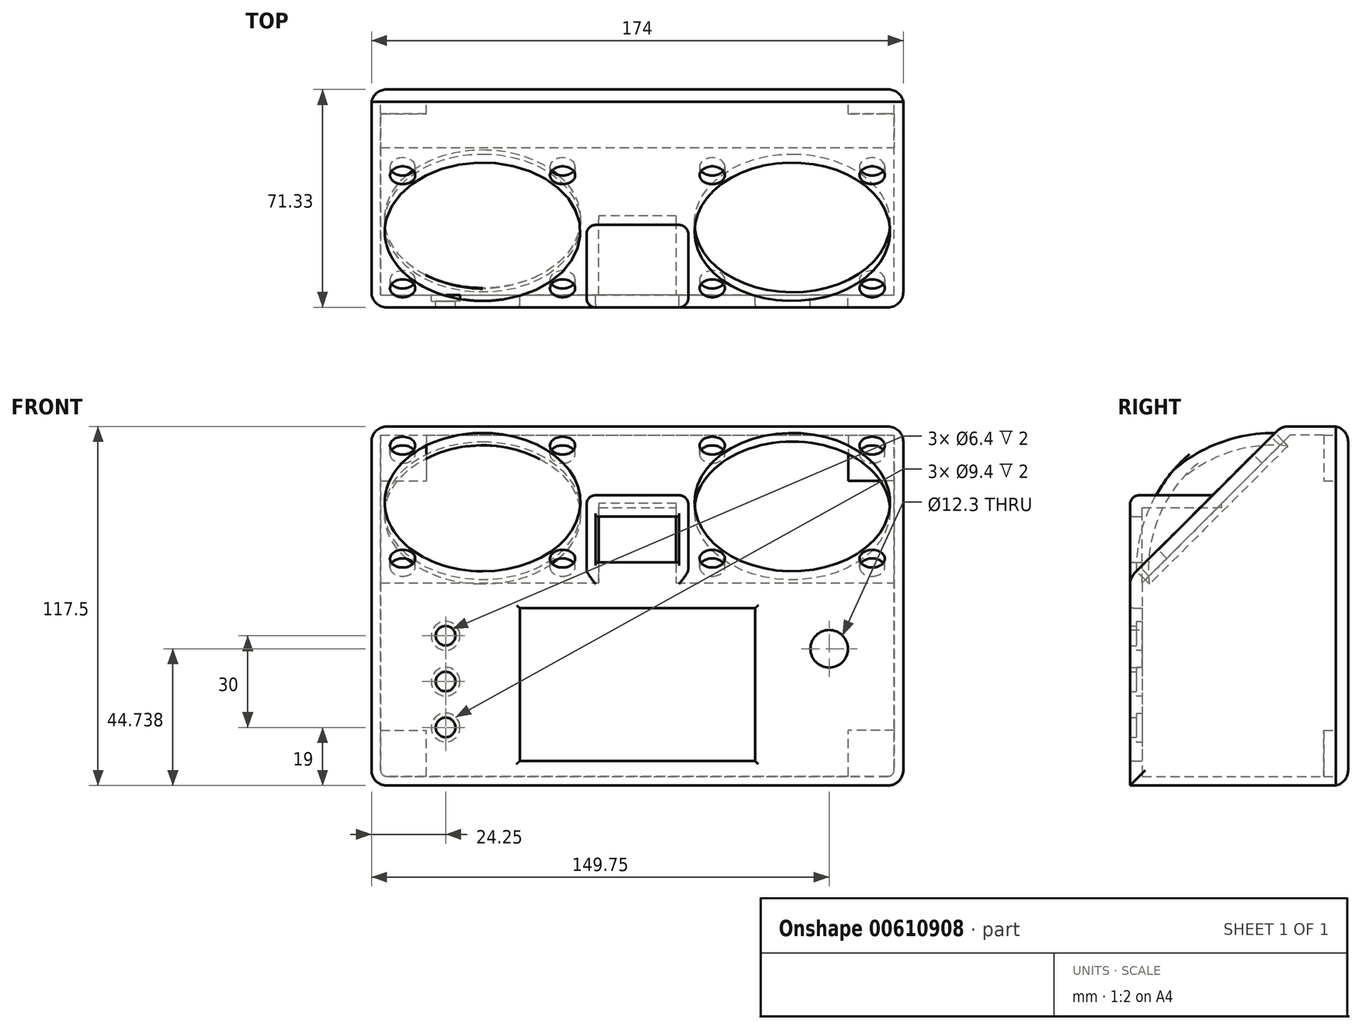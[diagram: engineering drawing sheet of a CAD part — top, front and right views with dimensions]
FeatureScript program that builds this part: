
annotation { "Feature Type Name" : "Feature", "Feature Type Description" : "" }
export const myFeature = defineFeature(function(context is Context, id is Id, definition is map)
    precondition{}
    {
        {
            assignVariable(context, id + "F0", {"name" : "thick", "anyValue" : 4});
        }
        {
            assignVariable(context, id + "F1", {"name" : "fillet_outer", "anyValue" : 5});
        }
        {
            var Q0;
            Q0=qCreatedBy(makeId("Front.planeOp"),FACE);
            var sketch = newSketch(context, id + "F2", { "sketchPlane" : qUnion([Q0])});
            skLineSegment(sketch, "E0.bottom", {"start": v(87, -34) * mm, "end": v(-87, -34) * mm});
            skLineSegment(sketch, "E0.left", {"start": v(87, -34) * mm, "end": v(87, 34) * mm});
            skLineSegment(sketch, "E0.right", {"start": v(-87, -34) * mm, "end": v(-87, 34) * mm});
            skPoint(sketch, "E0.middle", {"position": v(0, 0) * mm});
            skLineSegment(sketch, "E1.bottom", {"start": v(38.5, 24) * mm, "end": v(-38.5, 24) * mm});
            skLineSegment(sketch, "E1.top", {"start": v(38.5, -26) * mm, "end": v(-38.5, -26) * mm});
            skLineSegment(sketch, "E1.left", {"start": v(38.5, 24) * mm, "end": v(38.5, -26) * mm});
            skLineSegment(sketch, "E1.right", {"start": v(-38.5, 24) * mm, "end": v(-38.5, -26) * mm});
            skPoint(sketch, "E1.middle", {"position": v(0, -1) * mm});
            skLineSegment(sketch, "E2", {"start": v(-87, 34) * mm, "end": v(-16.65, 34) * mm});
            skLineSegment(sketch, "E3", {"start": v(-16.65, 34) * mm, "end": v(-16.65, 61) * mm});
            skLineSegment(sketch, "E4", {"start": v(-16.65, 61) * mm, "end": v(16.65, 61) * mm});
            skLineSegment(sketch, "E5", {"start": v(16.65, 61) * mm, "end": v(16.65, 34) * mm});
            skLineSegment(sketch, "E6", {"start": v(16.65, 34) * mm, "end": v(87, 34) * mm});
            skLineSegment(sketch, "E7.bottom", {"start": v(13.65, 39) * mm, "end": v(-13.65, 39) * mm});
            skLineSegment(sketch, "E7.top", {"start": v(13.65, 54) * mm, "end": v(-13.65, 54) * mm});
            skLineSegment(sketch, "E7.left", {"start": v(13.65, 39) * mm, "end": v(13.65, 54) * mm});
            skLineSegment(sketch, "E7.right", {"start": v(-13.65, 39) * mm, "end": v(-13.65, 54) * mm});
            skPoint(sketch, "E7.middle", {"position": v(0, 46.5) * mm});
            skPoint(sketch, "E8.visualSharp", {"position": v(-87, -34) * mm});
            skLineSegment(sketch, "E8.filletArc", {"start": v(-87, -34) * mm, "end": v(-87, -34) * mm});
            skPoint(sketch, "E9.visualSharp", {"position": v(87, -34) * mm});
            skLineSegment(sketch, "E9.filletArc", {"start": v(87, -34) * mm, "end": v(87, -34) * mm});
            skPoint(sketch, "E10.visualSharp", {"position": v(-16.65, 61) * mm});
            skLineSegment(sketch, "E10.filletArc", {"start": v(-16.65, 61) * mm, "end": v(-16.65, 61) * mm});
            skPoint(sketch, "E11.visualSharp", {"position": v(16.65, 61) * mm});
            skLineSegment(sketch, "E11.filletArc", {"start": v(16.65, 61) * mm, "end": v(16.65, 61) * mm});
            skPoint(sketch, "E12", {"position": v(-62.75, -15) * mm});
            skPoint(sketch, "E13.0.1.0", {"position": v(-62.75, 0) * mm});
            skPoint(sketch, "E13.0.2.0", {"position": v(-62.75, 15) * mm});
            skLineSegment(sketch, "E13.direction1", {"start": v(-62.75, -15) * mm, "end": v(80.58, -15) * mm, "construction": true});
            skLineSegment(sketch, "E13.direction2", {"start": v(-62.75, -15) * mm, "end": v(-62.75, 0) * mm, "construction": true});
            skCircle(sketch, "E14", {"center": v(62.75, 10.74) * mm, "radius": 6.15 * mm});
            skSolve(sketch);
        }
        {
            var Q0;
            Q0 = qSketchRegion(id + "F2", true);
            extrude(context, id + "F3", {"entities" : qUnion([Q0]), "depth" : (getVariable(context, 'thick')) * mm, "offsetDistance" : 25 * mm});
        }
        {
            var Q0;
            Q0=sQuery(id+"F2.wireOp",VERTEX,"E12");
            var Q1;
            Q1=sQuery(id+"F2.wireOp",VERTEX,"E13.0.1.0");
            var Q2;
            Q2=sQuery(id+"F2.wireOp",VERTEX,"E13.0.2.0");
            var Q3;
            Q3=makeQuery(id+"F3.opExtrude","SWEPT_BODY",BODY,{"disambiguationData":[OSD([sQuery(id+"F2.wireOp",EDGE,"E0.bottom"),sQuery(id+"F2.wireOp",EDGE,"E0.left"),sQuery(id+"F2.wireOp",EDGE,"E0.right"),sQuery(id+"F2.wireOp",EDGE,"E1.bottom"),sQuery(id+"F2.wireOp",EDGE,"E1.top"),sQuery(id+"F2.wireOp",EDGE,"E1.left"),sQuery(id+"F2.wireOp",EDGE,"E1.right"),sQuery(id+"F2.wireOp",EDGE,"E2"),sQuery(id+"F2.wireOp",EDGE,"E3"),sQuery(id+"F2.wireOp",EDGE,"E4"),sQuery(id+"F2.wireOp",EDGE,"E5"),sQuery(id+"F2.wireOp",EDGE,"E6"),sQuery(id+"F2.wireOp",EDGE,"E7.bottom"),sQuery(id+"F2.wireOp",EDGE,"E7.top"),sQuery(id+"F2.wireOp",EDGE,"E7.left"),sQuery(id+"F2.wireOp",EDGE,"E7.right"),sQuery(id+"F2.wireOp",EDGE,"E8.filletArc"),sQuery(id+"F2.wireOp",EDGE,"E9.filletArc"),sQuery(id+"F2.wireOp",EDGE,"E10.filletArc"),sQuery(id+"F2.wireOp",EDGE,"E11.filletArc")])]});
            hole(context, id + "F4", {"style" : HoleStyle.C_BORE, "endStyle" : HoleEndStyle.THROUGH, "oppositeDirection" : true, "holeDiameter" : 6.4 * mm, "cBoreDiameter" : 9.4 * mm, "cBoreDepth" : 2 * mm, "majorDiameter" : 5 * mm, "isTappedThrough" : true, "tappedDepth" : 12 * mm, "tapClearance" : 3, "startFromSketch" : true, "locations" : qUnion([Q0, Q1, Q2]), "scope" : qUnion([Q3])});
        }
        {
            var Q0;
            Q0=makeQuery(id+"F3.opExtrude","CAP_EDGE",EDGE,{"disambiguationData":[OSD([sQuery(id+"F2.wireOp",EDGE,"E2")])],"isStart":false});
            cPlane(context, id + "F5", {"entities" : qUnion([Q0]), "cplaneType" : CPlaneType.LINE_ANGLE, "offset" : 25 * mm, "angle" : 45 * degree, "oppositeDirection" : true, "flipAlignment" : true, "width" : 150 * mm, "height" : 150 * mm});
        }
        {
            var Q0;
            Q0=qCreatedBy(id+"F5.planeOp",FACE);
            var sketch = newSketch(context, id + "F6", { "sketchPlane" : qUnion([Q0])});
            skCircle(sketch, "E15", {"center": v(-50.65, 56.21) * mm, "radius": 32 * mm});
            skLineSegment(sketch, "E16.bottom", {"start": v(-16.65, 21.21) * mm, "end": v(-87, 21.21) * mm});
            skLineSegment(sketch, "E16.top", {"start": v(-16.65, 91.21) * mm, "end": v(-87, 91.21) * mm});
            skLineSegment(sketch, "E16.left", {"start": v(-16.65, 21.21) * mm, "end": v(-16.65, 91.21) * mm});
            skLineSegment(sketch, "E16.right", {"start": v(-87, 21.21) * mm, "end": v(-87, 91.21) * mm});
            skPoint(sketch, "E17.visualSharp", {"position": v(-87, 91.21) * mm});
            skLineSegment(sketch, "E17.filletArc", {"start": v(-87, 91.21) * mm, "end": v(-87, 91.21) * mm});
            skSolve(sketch);
        }
        {
            var Q0;
            Q0=qCreatedBy(id+"F5.planeOp",FACE);
            var sketch = newSketch(context, id + "F7", { "sketchPlane" : qUnion([Q0])});
            skLineSegment(sketch, "E18.bottom", {"start": v(16.65, 21.21) * mm, "end": v(87, 21.21) * mm});
            skLineSegment(sketch, "E18.top", {"start": v(16.65, 91.21) * mm, "end": v(87, 91.21) * mm});
            skLineSegment(sketch, "E18.left", {"start": v(16.65, 21.21) * mm, "end": v(16.65, 91.21) * mm});
            skLineSegment(sketch, "E18.right", {"start": v(87, 21.21) * mm, "end": v(87, 91.21) * mm});
            skCircle(sketch, "E19", {"center": v(50.65, 56.21) * mm, "radius": 32 * mm});
            skPoint(sketch, "E20.visualSharp", {"position": v(87, 91.21) * mm});
            skLineSegment(sketch, "E20.filletArc", {"start": v(87, 91.21) * mm, "end": v(87, 91.21) * mm});
            skSolve(sketch);
        }
        {
            var Q0;
            Q0=makeQuery(id+"F6.imprint","IMPRINT",FACE,{"disambiguationData":[TD([[makeQuery(id+"F6.imprint","IMPRINT",EDGE,{"derivedFrom":sQuery(id+"F6.wireOp",EDGE,"E15")}),-1.0]])]});
            var Q1;
            Q1=makeQuery(id+"F7.imprint","IMPRINT",FACE,{"disambiguationData":[TD([[makeQuery(id+"F7.imprint","IMPRINT",EDGE,{"derivedFrom":sQuery(id+"F7.wireOp",EDGE,"E18.bottom")}),1.0]])]});
            extrude(context, id + "F8", {"entities" : qUnion([Q0, Q1]), "operationType" : NewBodyOperationType.ADD, "depth" : (getVariable(context, 'thick')) * mm, "offsetDistance" : 25 * mm});
        }
        {
            var Q0;
            Q0=makeQuery(id+"F3.opExtrude","SWEPT_FACE",FACE,{"disambiguationData":[OSD([sQuery(id+"F2.wireOp",EDGE,"E3")])]});
            var sketch = newSketch(context, id + "F9", { "sketchPlane" : qUnion([Q0])});
            skLineSegment(sketch, "E21", {"start": v(0, 61) * mm, "end": v(-28.66, 61) * mm});
            skLineSegment(sketch, "E22", {"start": v(-28.66, 61) * mm, "end": v(0, 32.34) * mm});
            skLineSegment(sketch, "E23", {"start": v(0, 32.34) * mm, "end": v(0, 61) * mm});
            skSolve(sketch);
        }
        {
            var Q0;
            Q0 = qSketchRegion(id + "F9", true);
            extrude(context, id + "F10", {"entities" : qUnion([Q0]), "operationType" : NewBodyOperationType.ADD, "oppositeDirection" : true, "depth" : (getVariable(context, 'thick')) * mm, "offsetDistance" : 25 * mm});
        }
        {
            var Q0;
            Q0=makeQuery(id+"F3.opExtrude","SWEPT_FACE",FACE,{"disambiguationData":[OSD([sQuery(id+"F2.wireOp",EDGE,"E5")])]});
            var sketch = newSketch(context, id + "F11", { "sketchPlane" : qUnion([Q0])});
            skLineSegment(sketch, "E24", {"start": v(0, 61) * mm, "end": v(28.66, 61) * mm});
            skLineSegment(sketch, "E25", {"start": v(28.66, 61) * mm, "end": v(0, 32.34) * mm});
            skLineSegment(sketch, "E26", {"start": v(0, 32.34) * mm, "end": v(0, 61) * mm});
            skSolve(sketch);
        }
        {
            var Q0;
            Q0 = qSketchRegion(id + "F11", true);
            var Q1;
            Q1 = qConstructionFilter(qBodyType(qCreatedBy(id + "F11" ,EDGE), BodyType.WIRE), ConstructionObject.NO);
            extrude(context, id + "F12", {"entities" : qUnion([Q0]), "operationType" : NewBodyOperationType.ADD, "surfaceEntities" : qUnion([Q1]), "oppositeDirection" : true, "depth" : (getVariable(context, 'thick')) * mm, "offsetDistance" : 25 * mm});
        }
        {
            var Q0;
            Q0=makeQuery(id+"F8.opExtrude","CAP_FACE",FACE,{"disambiguationData":[OSD([sQuery(id+"F6.wireOp",EDGE,"E15"),sQuery(id+"F6.wireOp",EDGE,"E16.bottom"),sQuery(id+"F6.wireOp",EDGE,"E16.top"),sQuery(id+"F6.wireOp",EDGE,"E16.left"),sQuery(id+"F6.wireOp",EDGE,"E16.right"),sQuery(id+"F6.wireOp",EDGE,"E17.filletArc")])],"isStart":true});
            var sketch = newSketch(context, id + "F13", { "sketchPlane" : qUnion([Q0])});
            skLineSegment(sketch, "E27.bottom", {"start": v(16.65, 91.21) * mm, "end": v(-16.65, 91.21) * mm});
            skLineSegment(sketch, "E27.top", {"start": v(16.65, 59.4) * mm, "end": v(-16.65, 59.4) * mm});
            skLineSegment(sketch, "E27.left", {"start": v(16.65, 91.21) * mm, "end": v(16.65, 59.4) * mm});
            skLineSegment(sketch, "E27.right", {"start": v(-16.65, 91.21) * mm, "end": v(-16.65, 59.4) * mm});
            skSolve(sketch);
        }
        {
            var Q0;
            Q0=makeQuery(id+"F13.imprint","IMPRINT",FACE,{"disambiguationData":[TD([[makeQuery(id+"F13.imprint","IMPRINT",EDGE,{"derivedFrom":sQuery(id+"F13.wireOp",EDGE,"E27.bottom")}),1.0]])]});
            extrude(context, id + "F14", {"entities" : qUnion([Q0]), "operationType" : NewBodyOperationType.ADD, "oppositeDirection" : true, "depth" : (getVariable(context, 'thick')) * mm, "offsetDistance" : 25 * mm});
        }
        {
            var Q0;
            Q0=makeQuery(id+"F14.boolean.opBoolean","MERGE",FACE,{"derivedFrom":[makeQuery(id+"F8.opExtrude","CAP_FACE",FACE,{"disambiguationData":[OSD([sQuery(id+"F6.wireOp",EDGE,"E15"),sQuery(id+"F6.wireOp",EDGE,"E16.bottom"),sQuery(id+"F6.wireOp",EDGE,"E16.top"),sQuery(id+"F6.wireOp",EDGE,"E16.left"),sQuery(id+"F6.wireOp",EDGE,"E16.right")])],"isStart":true}),makeQuery(id+"F8.opExtrude","CAP_FACE",FACE,{"disambiguationData":[OSD([sQuery(id+"F7.wireOp",EDGE,"E18.bottom"),sQuery(id+"F7.wireOp",EDGE,"E18.top"),sQuery(id+"F7.wireOp",EDGE,"E18.left"),sQuery(id+"F7.wireOp",EDGE,"E18.right"),sQuery(id+"F7.wireOp",EDGE,"E19")])],"isStart":true}),makeQuery(id+"F14.opExtrude","CAP_FACE",FACE,{"disambiguationData":[OSD([sQuery(id+"F13.wireOp",EDGE,"E27.bottom"),sQuery(id+"F13.wireOp",EDGE,"E27.top"),sQuery(id+"F13.wireOp",EDGE,"E27.left"),sQuery(id+"F13.wireOp",EDGE,"E27.right")])],"isStart":true})]});
            var sketch = newSketch(context, id + "F15", { "sketchPlane" : qUnion([Q0])});
            skPoint(sketch, "E28", {"position": v(-76.81, 82.38) * mm});
            skPoint(sketch, "E29", {"position": v(-24.49, 82.38) * mm});
            skPoint(sketch, "E30", {"position": v(-24.49, 30.05) * mm});
            skPoint(sketch, "E31", {"position": v(-76.81, 30.05) * mm});
            skPoint(sketch, "E32", {"position": v(-50.65, 56.21) * mm});
            skPoint(sketch, "E33", {"position": v(24.49, 82.38) * mm});
            skPoint(sketch, "E34", {"position": v(76.81, 82.38) * mm});
            skPoint(sketch, "E35", {"position": v(76.81, 30.05) * mm});
            skPoint(sketch, "E36", {"position": v(24.49, 30.05) * mm});
            skPoint(sketch, "E37", {"position": v(50.65, 56.21) * mm});
            skCircle(sketch, "E38", {"center": v(-50.65, 56.21) * mm, "radius": 37 * mm, "construction": true});
            skCircle(sketch, "E39", {"center": v(50.65, 56.21) * mm, "radius": 37 * mm, "construction": true});
            skLineSegment(sketch, "E40", {"start": v(-50.65, 56.21) * mm, "end": v(-50.65, 93.21) * mm, "construction": true});
            skLineSegment(sketch, "E41", {"start": v(-50.65, 56.21) * mm, "end": v(-76.81, 82.38) * mm, "construction": true});
            skSolve(sketch);
        }
        {
            var Q0;
            Q0=sQuery(id+"F15.wireOp",VERTEX,"E28");
            var Q1;
            Q1=sQuery(id+"F15.wireOp",VERTEX,"E31");
            var Q2;
            Q2=sQuery(id+"F15.wireOp",VERTEX,"E29");
            var Q3;
            Q3=sQuery(id+"F15.wireOp",VERTEX,"E30");
            var Q4;
            Q4=sQuery(id+"F15.wireOp",VERTEX,"E36");
            var Q5;
            Q5=sQuery(id+"F15.wireOp",VERTEX,"E33");
            var Q6;
            Q6=sQuery(id+"F15.wireOp",VERTEX,"E34");
            var Q7;
            Q7=sQuery(id+"F15.wireOp",VERTEX,"E35");
            var Q8;
            Q8=makeQuery(id+"F3.opExtrude","SWEPT_BODY",BODY,{"disambiguationData":[OSD([sQuery(id+"F2.wireOp",EDGE,"E0.bottom"),sQuery(id+"F2.wireOp",EDGE,"E0.left"),sQuery(id+"F2.wireOp",EDGE,"E0.right"),sQuery(id+"F2.wireOp",EDGE,"E1.bottom"),sQuery(id+"F2.wireOp",EDGE,"E1.top"),sQuery(id+"F2.wireOp",EDGE,"E1.left"),sQuery(id+"F2.wireOp",EDGE,"E1.right"),sQuery(id+"F2.wireOp",EDGE,"E2"),sQuery(id+"F2.wireOp",EDGE,"E3"),sQuery(id+"F2.wireOp",EDGE,"E4"),sQuery(id+"F2.wireOp",EDGE,"E5"),sQuery(id+"F2.wireOp",EDGE,"E6"),sQuery(id+"F2.wireOp",EDGE,"E7.bottom"),sQuery(id+"F2.wireOp",EDGE,"E7.top"),sQuery(id+"F2.wireOp",EDGE,"E7.left"),sQuery(id+"F2.wireOp",EDGE,"E7.right")])]});
            hole(context, id + "F16", {"style" : HoleStyle.C_BORE, "endStyle" : HoleEndStyle.THROUGH, "standardTappedOrClearance" : lookupTablePath({ "standard" : "ISO", "fit" : "Close", "size" : "M4", "type" : "Clearance" }), "standardBlindInLast" : lookupTablePath({ "fit" : "Close", "standard" : "ISO", "size" : "M4", "type" : "Clearance" }), "holeDiameter" : 4.2 * mm, "cBoreDiameter" : 8.25 * mm, "cBoreDepth" : 4 * mm, "majorDiameter" : 5 * mm, "isTappedThrough" : true, "tappedDepth" : 12 * mm, "tapClearance" : 3, "startFromSketch" : true, "locations" : qUnion([Q0, Q1, Q2, Q3, Q4, Q5, Q6, Q7]), "scope" : qUnion([Q8])});
        }
        {
            var Q0;
            Q0=makeQuery(id+"F2.imprint","IMPRINT",FACE,{"disambiguationData":[TD([[makeQuery(id+"F2.imprint","IMPRINT",EDGE,{"derivedFrom":sQuery(id+"F2.wireOp",EDGE,"E0.bottom")}),-1.0]])]});
            var sketch = newSketch(context, id + "F17", { "sketchPlane" : qUnion([Q0])});
            skLineSegment(sketch, "E42", {"start": v(87, 32.34) * mm, "end": v(87, -34) * mm});
            skLineSegment(sketch, "E43", {"start": v(87, -34) * mm, "end": v(-87, -34) * mm});
            skLineSegment(sketch, "E44", {"start": v(-87, -34) * mm, "end": v(-87, 32.34) * mm});
            skLineSegment(sketch, "E45", {"start": v(-87, 32.34) * mm, "end": v(-84, 32.34) * mm});
            skLineSegment(sketch, "E46", {"start": v(-84, 32.34) * mm, "end": v(-84, -31) * mm});
            skLineSegment(sketch, "E47", {"start": v(-84, -31) * mm, "end": v(84, -31) * mm});
            skLineSegment(sketch, "E48", {"start": v(84, -31) * mm, "end": v(84, 32.34) * mm});
            skLineSegment(sketch, "E49", {"start": v(84, 32.34) * mm, "end": v(87, 32.34) * mm});
            skSolve(sketch);
        }
        {
            var Q0;
            Q0=makeQuery(id+"F2.imprint","IMPRINT",FACE,{"disambiguationData":[TD([[makeQuery(id+"F2.imprint","IMPRINT",EDGE,{"derivedFrom":sQuery(id+"F2.wireOp",EDGE,"E0.bottom")}),-1.0]])]});
            var Q1;
            Q1=makeQuery(id+"F14.boolean.opBoolean","MERGE",EDGE,{"derivedFrom":[makeQuery(id+"F8.opExtrude","CAP_EDGE",EDGE,{"disambiguationData":[OSD([sQuery(id+"F6.wireOp",EDGE,"E16.top")])],"isStart":false}),makeQuery(id+"F8.opExtrude","CAP_EDGE",EDGE,{"disambiguationData":[OSD([sQuery(id+"F7.wireOp",EDGE,"E18.top")])],"isStart":false}),makeQuery(id+"F14.opExtrude","CAP_EDGE",EDGE,{"disambiguationData":[OSD([sQuery(id+"F13.wireOp",EDGE,"E27.bottom")])],"isStart":false})]});
            cPlane(context, id + "F18", {"entities" : qUnion([Q0, Q1]), "cplaneType" : CPlaneType.LINE_ANGLE, "offset" : 50 * mm, "angle" : 0 * degree, "oppositeDirection" : true, "width" : 150 * mm, "height" : 150 * mm});
        }
        {
            var Q0;
            Q0=qCreatedBy(id+"F18.planeOp",FACE);
            var sketch = newSketch(context, id + "F19", { "sketchPlane" : qUnion([Q0])});
            skLineSegment(sketch, "E50", {"start": v(-87, 83.5) * mm, "end": v(-87, -34) * mm});
            skLineSegment(sketch, "E51", {"start": v(-87, -34) * mm, "end": v(87, -34) * mm});
            skLineSegment(sketch, "E52", {"start": v(87, -34) * mm, "end": v(87, 83.5) * mm});
            skLineSegment(sketch, "E53.0", {"start": v(84, -31) * mm, "end": v(84, 83.5) * mm});
            skLineSegment(sketch, "E53.1", {"start": v(-84, -31) * mm, "end": v(84, -31) * mm});
            skLineSegment(sketch, "E53.2", {"start": v(-84, 83.5) * mm, "end": v(-84, -31) * mm});
            skLineSegment(sketch, "E54", {"start": v(-87, 83.5) * mm, "end": v(-84, 83.5) * mm});
            skLineSegment(sketch, "E55", {"start": v(84, 83.5) * mm, "end": v(87, 83.5) * mm});
            skSolve(sketch);
        }
        {
            var Q1;
            Q1=makeQuery(id+"F17.imprint","IMPRINT",FACE,{"disambiguationData":[TD([[makeQuery(id+"F17.imprint","IMPRINT",EDGE,{"derivedFrom":sQuery(id+"F17.wireOp",EDGE,"E42")}),1.0]])]});
            var Q2;
            Q2=makeQuery(id+"F19.imprint","IMPRINT",FACE,{"disambiguationData":[TD([[makeQuery(id+"F19.imprint","IMPRINT",EDGE,{"derivedFrom":sQuery(id+"F19.wireOp",EDGE,"E50")}),1.0]])]});
            loft(context, id + "F20", {"operationType" : NewBodyOperationType.ADD, "sheetProfilesArray" : [{ "sheetProfileEntities" : qUnion([Q1]) }, { "sheetProfileEntities" : qUnion([Q2]) }]});
        }
        {
            var Q0;
            Q0=makeQuery(id+"F12.boolean.opBoolean","MERGE",FACE,{"derivedFrom":[makeQuery(id+"F10.boolean.opBoolean","MERGE",FACE,{"derivedFrom":[makeQuery(id+"F3.opExtrude","SWEPT_FACE",FACE,{"disambiguationData":[OSD([sQuery(id+"F2.wireOp",EDGE,"E4")])]}),makeQuery(id+"F10.opExtrude","SWEPT_FACE",FACE,{"disambiguationData":[OSD([sQuery(id+"F9.wireOp",EDGE,"E21")])]})]}),makeQuery(id+"F12.opExtrude","SWEPT_FACE",FACE,{"disambiguationData":[OSD([sQuery(id+"F11.wireOp",EDGE,"E24")])]})]});
            var sketch = newSketch(context, id + "F21", { "sketchPlane" : qUnion([Q0])});
            skLineSegment(sketch, "E56", {"start": v(-12.65, 26) * mm, "end": v(12.65, 26) * mm});
            skLineSegment(sketch, "E57", {"start": v(12.65, 26) * mm, "end": v(12.65, 0) * mm});
            skLineSegment(sketch, "E58", {"start": v(12.65, 0) * mm, "end": v(-12.65, 0) * mm});
            skLineSegment(sketch, "E59", {"start": v(-12.65, 0) * mm, "end": v(-12.65, 26) * mm});
            skSolve(sketch);
        }
        {
            var Q0;
            Q0 = qSketchRegion(id + "F21", true);
            extrude(context, id + "F22", {"entities" : qUnion([Q0]), "operationType" : NewBodyOperationType.ADD, "oppositeDirection" : true, "depth" : (getVariable(context, 'thick')) * mm, "offsetDistance" : 25 * mm});
        }
        {
            var Q0;
            {var subQ0=sQuery(id+"F2.wireOp",EDGE,"E0.right");Q0=makeQuery(id+"F20.boolean.opBoolean","MERGE",FACE,{"derivedFrom":[makeQuery(id+"F8.boolean.opBoolean","MERGE",FACE,{"derivedFrom":[makeQuery(id+"F3.opExtrude","SWEPT_FACE",FACE,{"disambiguationData":[OSD([subQ0])]}),makeQuery(id+"F8.opExtrude","SWEPT_FACE",FACE,{"disambiguationData":[OSD([sQuery(id+"F7.wireOp",EDGE,"E18.right")])]})]}),makeQuery(id+"F20.opLoft","SWEPT_FACE",FACE,{"disambiguationData":[OSD([subQ0,sQuery(id+"F17.wireOp",EDGE,"E43"),sQuery(id+"F17.wireOp",EDGE,"E44"),sQuery(id+"F17.wireOp",EDGE,"E45"),sQuery(id+"F19.wireOp",EDGE,"E51"),sQuery(id+"F19.wireOp",EDGE,"E52"),sQuery(id+"F19.wireOp",EDGE,"E55")])]})]});}
            var sketch = newSketch(context, id + "F23", { "sketchPlane" : qUnion([Q0])});
            skLineSegment(sketch, "E60", {"start": v(-45.5, 83.5) * mm, "end": v(-48.33, 83.5) * mm});
            skLineSegment(sketch, "E61", {"start": v(-48.33, 83.5) * mm, "end": v(-48.33, 80.67) * mm});
            skLineSegment(sketch, "E62", {"start": v(-48.33, 80.67) * mm, "end": v(-45.5, 80.67) * mm});
            skLineSegment(sketch, "E63", {"start": v(-45.5, 80.67) * mm, "end": v(-45.5, 83.5) * mm});
            skSolve(sketch);
        }
        {
            var Q0;
            Q0 = qSketchRegion(id + "F23", true);
            var Q1;
            {var subQ0=sQuery(id+"F2.wireOp",EDGE,"E0.left");Q1=makeQuery(id+"F20.boolean.opBoolean","MERGE",FACE,{"derivedFrom":[makeQuery(id+"F8.boolean.opBoolean","MERGE",FACE,{"derivedFrom":[makeQuery(id+"F3.opExtrude","SWEPT_FACE",FACE,{"disambiguationData":[OSD([subQ0])]}),makeQuery(id+"F8.opExtrude","SWEPT_FACE",FACE,{"disambiguationData":[OSD([sQuery(id+"F6.wireOp",EDGE,"E16.right")])]})]}),makeQuery(id+"F20.opLoft","SWEPT_FACE",FACE,{"disambiguationData":[OSD([subQ0,sQuery(id+"F17.wireOp",EDGE,"E42"),sQuery(id+"F17.wireOp",EDGE,"E43"),sQuery(id+"F17.wireOp",EDGE,"E49"),sQuery(id+"F19.wireOp",EDGE,"E50"),sQuery(id+"F19.wireOp",EDGE,"E51"),sQuery(id+"F19.wireOp",EDGE,"E54")])]})]});}
            extrude(context, id + "F24", {"entities" : qUnion([Q0]), "operationType" : NewBodyOperationType.ADD, "endBound" : BoundingType.UP_TO_SURFACE, "oppositeDirection" : true, "depth" : 25 * mm, "endBoundEntityFace" : qUnion([Q1]), "offsetDistance" : 25 * mm});
        }
        {
            var Q0;
            Q0=makeQuery(id+"F24.boolean.opBoolean","MERGE",FACE,{"derivedFrom":[makeQuery(id+"F20.opLoft","CAP_FACE",FACE,{"disambiguationData":[OSD([makeQuery(id+"F19.imprint","IMPRINT",FACE,{"disambiguationData":[TD([[makeQuery(id+"F19.imprint","IMPRINT",EDGE,{"derivedFrom":sQuery(id+"F19.wireOp",EDGE,"E50")}),1.0]])]})])],"isStart":true}),makeQuery(id+"F24.opExtrude","SWEPT_FACE",FACE,{"disambiguationData":[OSD([sQuery(id+"F23.wireOp",EDGE,"E61")])]})]});
            var sketch = newSketch(context, id + "F25", { "sketchPlane" : qUnion([Q0])});
            skLineSegment(sketch, "E64", {"start": v(-87, 83.5) * mm, "end": v(-87, -34) * mm});
            skLineSegment(sketch, "E65", {"start": v(-87, -34) * mm, "end": v(87, -34) * mm});
            skLineSegment(sketch, "E66", {"start": v(87, -34) * mm, "end": v(87, 83.5) * mm});
            skLineSegment(sketch, "E67", {"start": v(87, 83.5) * mm, "end": v(-87, 83.5) * mm});
            skLineSegment(sketch, "E68", {"start": v(-84, 80.67) * mm, "end": v(-84, -31) * mm});
            skLineSegment(sketch, "E69", {"start": v(-84, -31) * mm, "end": v(84, -31) * mm});
            skLineSegment(sketch, "E70", {"start": v(84, -31) * mm, "end": v(84, 80.67) * mm});
            skLineSegment(sketch, "E71", {"start": v(84, 80.67) * mm, "end": v(-84, 80.67) * mm});
            skSolve(sketch);
        }
        {
            var Q0;
            Q0 = qSketchRegion(id + "F25", true);
            extrude(context, id + "F26", {"entities" : qUnion([Q0]), "operationType" : NewBodyOperationType.ADD, "depth" : 15 * mm, "offsetDistance" : 25 * mm});
        }
        {
            var Q0;
            Q0=makeQuery(id+"F26.opExtrude","CAP_FACE",FACE,{"disambiguationData":[OSD([sQuery(id+"F25.wireOp",EDGE,"E64"),sQuery(id+"F25.wireOp",EDGE,"E65"),sQuery(id+"F25.wireOp",EDGE,"E66"),sQuery(id+"F25.wireOp",EDGE,"E67"),sQuery(id+"F25.wireOp",EDGE,"E68"),sQuery(id+"F25.wireOp",EDGE,"E69"),sQuery(id+"F25.wireOp",EDGE,"E70"),sQuery(id+"F25.wireOp",EDGE,"E71")])],"isStart":false});
            var sketch = newSketch(context, id + "F27", { "sketchPlane" : qUnion([Q0])});
            skLineSegment(sketch, "E72.bottom", {"start": v(-84, 80.67) * mm, "end": v(-69, 80.67) * mm});
            skLineSegment(sketch, "E72.top", {"start": v(-84, 65.67) * mm, "end": v(-69, 65.67) * mm});
            skLineSegment(sketch, "E72.left", {"start": v(-84, 80.67) * mm, "end": v(-84, 65.67) * mm});
            skLineSegment(sketch, "E72.right", {"start": v(-69, 80.67) * mm, "end": v(-69, 65.67) * mm});
            skLineSegment(sketch, "E73.bottom", {"start": v(-84, -31) * mm, "end": v(-69, -31) * mm});
            skLineSegment(sketch, "E73.top", {"start": v(-84, -16) * mm, "end": v(-69, -16) * mm});
            skLineSegment(sketch, "E73.left", {"start": v(-84, -31) * mm, "end": v(-84, -16) * mm});
            skLineSegment(sketch, "E73.right", {"start": v(-69, -31) * mm, "end": v(-69, -16) * mm});
            skLineSegment(sketch, "E74.MirrorCS", {"start": v(84, -16) * mm, "end": v(69, -16) * mm});
            skLineSegment(sketch, "E75.MirrorCS", {"start": v(69, -31) * mm, "end": v(69, -16) * mm});
            skLineSegment(sketch, "E76.MirrorCS", {"start": v(84, -31) * mm, "end": v(69, -31) * mm});
            skLineSegment(sketch, "E77.MirrorCS", {"start": v(84, -31) * mm, "end": v(84, -16) * mm});
            skLineSegment(sketch, "E78.MirrorCS", {"start": v(69, 80.67) * mm, "end": v(69, 65.67) * mm});
            skLineSegment(sketch, "E79.MirrorCS", {"start": v(84, 80.67) * mm, "end": v(69, 80.67) * mm});
            skLineSegment(sketch, "E80.MirrorCS", {"start": v(84, 65.67) * mm, "end": v(69, 65.67) * mm});
            skLineSegment(sketch, "E81.MirrorCS", {"start": v(84, 80.67) * mm, "end": v(84, 65.67) * mm});
            skSolve(sketch);
        }
        {
            var Q0;
            Q0 = qSketchRegion(id + "F27", true);
            extrude(context, id + "F28", {"entities" : qUnion([Q0]), "operationType" : NewBodyOperationType.ADD, "oppositeDirection" : true, "depth" : (getVariable(context, 'thick')) * mm, "offsetDistance" : 25 * mm});
        }
        {
            var Q0;
            Q0=makeQuery(id+"F28.boolean.opBoolean","MERGE",FACE,{"derivedFrom":[makeQuery(id+"F26.opExtrude","CAP_FACE",FACE,{"disambiguationData":[OSD([sQuery(id+"F25.wireOp",EDGE,"E64"),sQuery(id+"F25.wireOp",EDGE,"E65"),sQuery(id+"F25.wireOp",EDGE,"E66"),sQuery(id+"F25.wireOp",EDGE,"E67"),sQuery(id+"F25.wireOp",EDGE,"E68"),sQuery(id+"F25.wireOp",EDGE,"E69"),sQuery(id+"F25.wireOp",EDGE,"E70"),sQuery(id+"F25.wireOp",EDGE,"E71")])],"isStart":false}),makeQuery(id+"F28.opExtrude","CAP_FACE",FACE,{"disambiguationData":[OSD([sQuery(id+"F27.wireOp",EDGE,"E72.bottom"),sQuery(id+"F27.wireOp",EDGE,"E72.top"),sQuery(id+"F27.wireOp",EDGE,"E72.left"),sQuery(id+"F27.wireOp",EDGE,"E72.right")])],"isStart":true}),makeQuery(id+"F28.opExtrude","CAP_FACE",FACE,{"disambiguationData":[OSD([sQuery(id+"F27.wireOp",EDGE,"E73.bottom"),sQuery(id+"F27.wireOp",EDGE,"E73.top"),sQuery(id+"F27.wireOp",EDGE,"E73.left"),sQuery(id+"F27.wireOp",EDGE,"E73.right")])],"isStart":true}),makeQuery(id+"F28.opExtrude","CAP_FACE",FACE,{"disambiguationData":[OSD([sQuery(id+"F27.wireOp",EDGE,"E74.MirrorCS"),sQuery(id+"F27.wireOp",EDGE,"E75.MirrorCS"),sQuery(id+"F27.wireOp",EDGE,"E76.MirrorCS"),sQuery(id+"F27.wireOp",EDGE,"E77.MirrorCS")])],"isStart":true}),makeQuery(id+"F28.opExtrude","CAP_FACE",FACE,{"disambiguationData":[OSD([sQuery(id+"F27.wireOp",EDGE,"E78.MirrorCS"),sQuery(id+"F27.wireOp",EDGE,"E79.MirrorCS"),sQuery(id+"F27.wireOp",EDGE,"E80.MirrorCS"),sQuery(id+"F27.wireOp",EDGE,"E81.MirrorCS")])],"isStart":true})]});
            var sketch = newSketch(context, id + "F29", { "sketchPlane" : qUnion([Q0])});
            skLineSegment(sketch, "E82.bottom", {"start": v(-82, 83.5) * mm, "end": v(82, 83.5) * mm});
            skLineSegment(sketch, "E82.top", {"start": v(-82, -34) * mm, "end": v(82, -34) * mm});
            skLineSegment(sketch, "E82.left", {"start": v(-87, 78.5) * mm, "end": v(-87, -29) * mm});
            skLineSegment(sketch, "E82.right", {"start": v(87, 78.5) * mm, "end": v(87, -29) * mm});
            skPoint(sketch, "E83.visualSharp", {"position": v(-87, -34) * mm});
            skArc(sketch, "E83.filletArc", {"start": v(-87, -29) * mm, "mid": v(-85.54, -32.54) * mm, "end": v(-82, -34) * mm});
            skPoint(sketch, "E84.visualSharp", {"position": v(-87, 83.5) * mm});
            skArc(sketch, "E84.filletArc", {"start": v(-82, 83.5) * mm, "mid": v(-85.54, 82.03) * mm, "end": v(-87, 78.5) * mm});
            skPoint(sketch, "E85.visualSharp", {"position": v(87, 83.5) * mm});
            skArc(sketch, "E85.filletArc", {"start": v(87, 78.5) * mm, "mid": v(85.54, 82.03) * mm, "end": v(82, 83.5) * mm});
            skPoint(sketch, "E86.visualSharp", {"position": v(87, -34) * mm});
            skArc(sketch, "E86.filletArc", {"start": v(82, -34) * mm, "mid": v(85.54, -32.54) * mm, "end": v(87, -29) * mm});
            skSolve(sketch);
        }
        {
            var Q0;
            Q0 = qSketchRegion(id + "F29", true);
            extrude(context, id + "F30", {"entities" : qUnion([Q0]), "depth" : (getVariable(context, 'thick')) * mm, "offsetDistance" : 25 * mm});
        }
        {
            var Q0;
            Q0=makeQuery(id+"F8.opExtrude","CAP_EDGE",EDGE,{"disambiguationData":[OSD([sQuery(id+"F7.wireOp",EDGE,"E18.right")])],"isStart":true});
            var Q1;
            Q1=makeQuery(id+"F3.opExtrude","CAP_EDGE",EDGE,{"disambiguationData":[OSD([sQuery(id+"F2.wireOp",EDGE,"E0.right")])],"isStart":false});
            var Q2;
            Q2=makeQuery(id+"F20.boolean.opBoolean","MERGE",EDGE,{"derivedFrom":[makeQuery(id+"F3.opExtrude","SWEPT_EDGE",EDGE,{"disambiguationData":[OSD([sQuery(id+"F2.wireOp",EDGE,"E0.bottom"),sQuery(id+"F2.wireOp",EDGE,"E0.right")])]}),makeQuery(id+"F20.opLoft","SWEPT_EDGE",EDGE,{"disambiguationData":[OSD([sQuery(id+"F17.wireOp",EDGE,"E43"),sQuery(id+"F17.wireOp",EDGE,"E44"),sQuery(id+"F19.wireOp",EDGE,"E51"),sQuery(id+"F19.wireOp",EDGE,"E52")])]})]});
            var Q3;
            Q3=makeQuery(id+"F20.boolean.opBoolean","MERGE",EDGE,{"derivedFrom":[makeQuery(id+"F3.opExtrude","SWEPT_EDGE",EDGE,{"disambiguationData":[OSD([sQuery(id+"F2.wireOp",EDGE,"E0.bottom"),sQuery(id+"F2.wireOp",EDGE,"E0.left")])]}),makeQuery(id+"F20.opLoft","SWEPT_EDGE",EDGE,{"disambiguationData":[OSD([sQuery(id+"F17.wireOp",EDGE,"E42"),sQuery(id+"F17.wireOp",EDGE,"E43"),sQuery(id+"F19.wireOp",EDGE,"E50"),sQuery(id+"F19.wireOp",EDGE,"E51")])]})]});
            var Q4;
            Q4=makeQuery(id+"F3.opExtrude","CAP_EDGE",EDGE,{"disambiguationData":[OSD([sQuery(id+"F2.wireOp",EDGE,"E0.left")])],"isStart":false});
            var Q5;
            Q5=makeQuery(id+"F8.opExtrude","CAP_EDGE",EDGE,{"disambiguationData":[OSD([sQuery(id+"F6.wireOp",EDGE,"E16.right")])],"isStart":true});
            var Q6;
            Q6=makeQuery(id+"F8.boolean.opBoolean","MERGE",EDGE,{"derivedFrom":[makeQuery(id+"F3.opExtrude","CAP_EDGE",EDGE,{"disambiguationData":[OSD([sQuery(id+"F2.wireOp",EDGE,"E2")])],"isStart":false}),makeQuery(id+"F8.opExtrude","CAP_EDGE",EDGE,{"disambiguationData":[OSD([sQuery(id+"F7.wireOp",EDGE,"E18.bottom")])],"isStart":true})]});
            var Q7;
            Q7=makeQuery(id+"F8.boolean.opBoolean","MERGE",EDGE,{"derivedFrom":[makeQuery(id+"F3.opExtrude","CAP_EDGE",EDGE,{"disambiguationData":[OSD([sQuery(id+"F2.wireOp",EDGE,"E6")])],"isStart":false}),makeQuery(id+"F8.opExtrude","CAP_EDGE",EDGE,{"disambiguationData":[OSD([sQuery(id+"F6.wireOp",EDGE,"E16.bottom")])],"isStart":true})]});
            var Q8;
            {var subQ0=sQuery(id+"F7.wireOp",EDGE,"E18.top");Q8=makeQuery(id+"F24.boolean.opBoolean","MERGE",EDGE,{"derivedFrom":[makeQuery(id+"F14.boolean.opBoolean","MERGE",EDGE,{"derivedFrom":[makeQuery(id+"F8.opExtrude","CAP_EDGE",EDGE,{"disambiguationData":[OSD([sQuery(id+"F6.wireOp",EDGE,"E16.top")])],"isStart":true}),makeQuery(id+"F8.opExtrude","CAP_EDGE",EDGE,{"disambiguationData":[OSD([subQ0])],"isStart":true}),makeQuery(id+"F14.opExtrude","CAP_EDGE",EDGE,{"disambiguationData":[OSD([sQuery(id+"F13.wireOp",EDGE,"E27.bottom")])],"isStart":true})]}),makeQuery(id+"F24.opExtrude","SWEPT_EDGE",EDGE,{"disambiguationData":[OSD([subQ0,sQuery(id+"F7.wireOp",EDGE,"E18.right"),sQuery(id+"F23.wireOp",EDGE,"E60"),sQuery(id+"F23.wireOp",EDGE,"E63")])]})]});}
            var Q9;
            Q9=makeQuery(id+"F26.boolean.opBoolean","MERGE",EDGE,{"derivedFrom":[makeQuery(id+"F24.opExtrude","CAP_EDGE",EDGE,{"disambiguationData":[OSD([sQuery(id+"F23.wireOp",EDGE,"E60")])],"isStart":false}),makeQuery(id+"F26.opExtrude","SWEPT_EDGE",EDGE,{"disambiguationData":[OSD([sQuery(id+"F25.wireOp",EDGE,"E64"),sQuery(id+"F25.wireOp",EDGE,"E67")])]})]});
            var Q10;
            Q10=makeQuery(id+"F26.boolean.opBoolean","MERGE",EDGE,{"derivedFrom":[makeQuery(id+"F24.opExtrude","CAP_EDGE",EDGE,{"disambiguationData":[OSD([sQuery(id+"F23.wireOp",EDGE,"E60")])],"isStart":true}),makeQuery(id+"F26.opExtrude","SWEPT_EDGE",EDGE,{"disambiguationData":[OSD([sQuery(id+"F25.wireOp",EDGE,"E66"),sQuery(id+"F25.wireOp",EDGE,"E67")])]})]});
            var Q11;
            Q11=makeQuery(id+"F30.opExtrude","CAP_EDGE",EDGE,{"disambiguationData":[OSD([sQuery(id+"F29.wireOp",EDGE,"E82.left")])],"isStart":false});
            fillet(context, id + "F31", {"entities" : qUnion([Q0, Q1, Q2, Q3, Q4, Q5, Q6, Q7, Q8, Q9, Q10, Q11]), "radius" : (getVariable(context, 'fillet_outer')) * mm, "tangentPropagation" : true, "allowEdgeOverflow" : false});
        }
        {
            var Q0;
            Q0=makeQuery(id+"F3.opExtrude","CAP_EDGE",EDGE,{"disambiguationData":[OSD([sQuery(id+"F2.wireOp",EDGE,"E3")])],"isStart":false});
            var Q1;
            Q1=makeQuery(id+"F3.opExtrude","CAP_EDGE",EDGE,{"disambiguationData":[OSD([sQuery(id+"F2.wireOp",EDGE,"E5")])],"isStart":false});
            var Q2;
            Q2=makeQuery(id+"F3.opExtrude","CAP_EDGE",EDGE,{"disambiguationData":[OSD([sQuery(id+"F2.wireOp",EDGE,"E4")])],"isStart":false});
            var Q3;
            Q3=makeQuery(id+"F10.boolean.opBoolean","MERGE",EDGE,{"derivedFrom":[makeQuery(id+"F3.opExtrude","SWEPT_EDGE",EDGE,{"disambiguationData":[OSD([sQuery(id+"F2.wireOp",EDGE,"E3"),sQuery(id+"F2.wireOp",EDGE,"E4")])]}),makeQuery(id+"F10.opExtrude","CAP_EDGE",EDGE,{"disambiguationData":[OSD([sQuery(id+"F9.wireOp",EDGE,"E21")])],"isStart":true})]});
            var Q4;
            Q4=makeQuery(id+"F12.boolean.opBoolean","MERGE",EDGE,{"derivedFrom":[makeQuery(id+"F3.opExtrude","SWEPT_EDGE",EDGE,{"disambiguationData":[OSD([sQuery(id+"F2.wireOp",EDGE,"E4"),sQuery(id+"F2.wireOp",EDGE,"E5")])]}),makeQuery(id+"F12.opExtrude","CAP_EDGE",EDGE,{"disambiguationData":[OSD([sQuery(id+"F11.wireOp",EDGE,"E24")])],"isStart":true})]});
            fillet(context, id + "F32", {"entities" : qUnion([Q0, Q1, Q2, Q3, Q4]), "radius" : 3 * mm, "tangentPropagation" : true, "allowEdgeOverflow" : false});
        }
        {
            var Q0;
            Q0=makeQuery(id+"F3.opExtrude","CAP_EDGE",EDGE,{"disambiguationData":[OSD([sQuery(id+"F2.wireOp",EDGE,"E1.right")])],"isStart":false});
            var Q1;
            Q1=makeQuery(id+"F3.opExtrude","CAP_EDGE",EDGE,{"disambiguationData":[OSD([sQuery(id+"F2.wireOp",EDGE,"E1.bottom")])],"isStart":false});
            var Q2;
            Q2=makeQuery(id+"F3.opExtrude","CAP_EDGE",EDGE,{"disambiguationData":[OSD([sQuery(id+"F2.wireOp",EDGE,"E1.left")])],"isStart":false});
            var Q3;
            Q3=makeQuery(id+"F3.opExtrude","CAP_EDGE",EDGE,{"disambiguationData":[OSD([sQuery(id+"F2.wireOp",EDGE,"E1.top")])],"isStart":false});
            var Q4;
            Q4=makeQuery(id+"F32.opFillet","BLEND_EDGE",EDGE,{"blendedFrom":[makeQuery(id+"F3.opExtrude","CAP_EDGE",EDGE,{"disambiguationData":[OSD([sQuery(id+"F2.wireOp",EDGE,"E3")])],"isStart":false}),makeQuery(id+"F10.boolean.opBoolean","MERGE",FACE,{"derivedFrom":[makeQuery(id+"F3.opExtrude","SWEPT_FACE",FACE,{"disambiguationData":[OSD([sQuery(id+"F2.wireOp",EDGE,"E7.right")])]}),makeQuery(id+"F10.opExtrude","CAP_FACE",FACE,{"disambiguationData":[OSD([sQuery(id+"F9.wireOp",EDGE,"E21"),sQuery(id+"F9.wireOp",EDGE,"E22"),sQuery(id+"F9.wireOp",EDGE,"E23")])],"isStart":false})]})],"blendedInto":[makeQuery(id+"F10.boolean.opBoolean","MERGE",FACE,{"derivedFrom":[makeQuery(id+"F3.opExtrude","SWEPT_FACE",FACE,{"disambiguationData":[OSD([sQuery(id+"F2.wireOp",EDGE,"E7.right")])]}),makeQuery(id+"F10.opExtrude","CAP_FACE",FACE,{"disambiguationData":[OSD([sQuery(id+"F9.wireOp",EDGE,"E21"),sQuery(id+"F9.wireOp",EDGE,"E22"),sQuery(id+"F9.wireOp",EDGE,"E23")])],"isStart":false})]})]});
            var Q5;
            Q5=makeQuery(id+"F3.opExtrude","CAP_EDGE",EDGE,{"disambiguationData":[OSD([sQuery(id+"F2.wireOp",EDGE,"E7.bottom")])],"isStart":false});
            var Q6;
            Q6=makeQuery(id+"F32.opFillet","BLEND_EDGE",EDGE,{"blendedFrom":[makeQuery(id+"F3.opExtrude","CAP_EDGE",EDGE,{"disambiguationData":[OSD([sQuery(id+"F2.wireOp",EDGE,"E5")])],"isStart":false}),makeQuery(id+"F12.boolean.opBoolean","MERGE",FACE,{"derivedFrom":[makeQuery(id+"F3.opExtrude","SWEPT_FACE",FACE,{"disambiguationData":[OSD([sQuery(id+"F2.wireOp",EDGE,"E7.left")])]}),makeQuery(id+"F12.opExtrude","CAP_FACE",FACE,{"disambiguationData":[OSD([sQuery(id+"F11.wireOp",EDGE,"E24"),sQuery(id+"F11.wireOp",EDGE,"E25"),sQuery(id+"F11.wireOp",EDGE,"E26")])],"isStart":false})]})],"blendedInto":[makeQuery(id+"F12.boolean.opBoolean","MERGE",FACE,{"derivedFrom":[makeQuery(id+"F3.opExtrude","SWEPT_FACE",FACE,{"disambiguationData":[OSD([sQuery(id+"F2.wireOp",EDGE,"E7.left")])]}),makeQuery(id+"F12.opExtrude","CAP_FACE",FACE,{"disambiguationData":[OSD([sQuery(id+"F11.wireOp",EDGE,"E24"),sQuery(id+"F11.wireOp",EDGE,"E25"),sQuery(id+"F11.wireOp",EDGE,"E26")])],"isStart":false})]})]});
            var Q7;
            Q7=makeQuery(id+"F3.opExtrude","CAP_EDGE",EDGE,{"disambiguationData":[OSD([sQuery(id+"F2.wireOp",EDGE,"E7.top")])],"isStart":false});
            fillet(context, id + "F33", {"entities" : qUnion([Q0, Q1, Q2, Q3, Q4, Q5, Q6, Q7]), "radius" : 1 * mm, "tangentPropagation" : true, "allowEdgeOverflow" : false});
        }
        {
            var Q0;
            Q0=makeQuery(id+"F20.opLoft","SWEPT_EDGE",EDGE,{"disambiguationData":[OSD([sQuery(id+"F17.wireOp",EDGE,"E47"),sQuery(id+"F17.wireOp",EDGE,"E48"),sQuery(id+"F19.wireOp",EDGE,"E53.1"),sQuery(id+"F19.wireOp",EDGE,"E53.2")])]});
            var Q1;
            Q1=makeQuery(id+"F20.opLoft","SWEPT_EDGE",EDGE,{"disambiguationData":[OSD([sQuery(id+"F17.wireOp",EDGE,"E46"),sQuery(id+"F17.wireOp",EDGE,"E47"),sQuery(id+"F19.wireOp",EDGE,"E53.0"),sQuery(id+"F19.wireOp",EDGE,"E53.1")])]});
            var Q2;
            Q2=makeQuery(id+"F20.opLoft","MID_CAP_EDGE",EDGE,{"disambiguationData":[OSD([sQuery(id+"F17.wireOp",EDGE,"E45"),sQuery(id+"F17.wireOp",EDGE,"E46"),sQuery(id+"F17.wireOp",EDGE,"E47")])],"capPos":0.0});
            var Q3;
            Q3=makeQuery(id+"F20.opLoft","MID_CAP_EDGE",EDGE,{"disambiguationData":[OSD([sQuery(id+"F17.wireOp",EDGE,"E47"),sQuery(id+"F17.wireOp",EDGE,"E48"),sQuery(id+"F17.wireOp",EDGE,"E49")])],"capPos":0.0});
            var Q4;
            Q4=makeQuery(id+"F12.boolean.opBoolean","MERGE",EDGE,{"derivedFrom":[makeQuery(id+"F8.boolean.opBoolean","INTERSECT",EDGE,{"derivedFrom":[makeQuery(id+"F3.opExtrude","CAP_FACE",FACE,{"disambiguationData":[OSD([sQuery(id+"F2.wireOp",EDGE,"E0.bottom"),sQuery(id+"F2.wireOp",EDGE,"E0.left"),sQuery(id+"F2.wireOp",EDGE,"E0.right"),sQuery(id+"F2.wireOp",EDGE,"E1.bottom"),sQuery(id+"F2.wireOp",EDGE,"E1.top"),sQuery(id+"F2.wireOp",EDGE,"E1.left"),sQuery(id+"F2.wireOp",EDGE,"E1.right"),sQuery(id+"F2.wireOp",EDGE,"E2"),sQuery(id+"F2.wireOp",EDGE,"E3"),sQuery(id+"F2.wireOp",EDGE,"E4"),sQuery(id+"F2.wireOp",EDGE,"E5"),sQuery(id+"F2.wireOp",EDGE,"E6"),sQuery(id+"F2.wireOp",EDGE,"E7.bottom"),sQuery(id+"F2.wireOp",EDGE,"E7.top"),sQuery(id+"F2.wireOp",EDGE,"E7.left"),sQuery(id+"F2.wireOp",EDGE,"E7.right")])],"isStart":true}),makeQuery(id+"F8.opExtrude","CAP_FACE",FACE,{"disambiguationData":[OSD([sQuery(id+"F6.wireOp",EDGE,"E15"),sQuery(id+"F6.wireOp",EDGE,"E16.bottom"),sQuery(id+"F6.wireOp",EDGE,"E16.top"),sQuery(id+"F6.wireOp",EDGE,"E16.left"),sQuery(id+"F6.wireOp",EDGE,"E16.right")])],"isStart":false})]}),makeQuery(id+"F12.opExtrude","SWEPT_EDGE",EDGE,{"disambiguationData":[OSD([sQuery(id+"F11.wireOp",EDGE,"E25"),sQuery(id+"F11.wireOp",EDGE,"E26")])]})]});
            var Q5;
            Q5=makeQuery(id+"F10.boolean.opBoolean","MERGE",EDGE,{"derivedFrom":[makeQuery(id+"F8.boolean.opBoolean","INTERSECT",EDGE,{"derivedFrom":[makeQuery(id+"F3.opExtrude","CAP_FACE",FACE,{"disambiguationData":[OSD([sQuery(id+"F2.wireOp",EDGE,"E0.bottom"),sQuery(id+"F2.wireOp",EDGE,"E0.left"),sQuery(id+"F2.wireOp",EDGE,"E0.right"),sQuery(id+"F2.wireOp",EDGE,"E1.bottom"),sQuery(id+"F2.wireOp",EDGE,"E1.top"),sQuery(id+"F2.wireOp",EDGE,"E1.left"),sQuery(id+"F2.wireOp",EDGE,"E1.right"),sQuery(id+"F2.wireOp",EDGE,"E2"),sQuery(id+"F2.wireOp",EDGE,"E3"),sQuery(id+"F2.wireOp",EDGE,"E4"),sQuery(id+"F2.wireOp",EDGE,"E5"),sQuery(id+"F2.wireOp",EDGE,"E6"),sQuery(id+"F2.wireOp",EDGE,"E7.bottom"),sQuery(id+"F2.wireOp",EDGE,"E7.top"),sQuery(id+"F2.wireOp",EDGE,"E7.left"),sQuery(id+"F2.wireOp",EDGE,"E7.right")])],"isStart":true}),makeQuery(id+"F8.opExtrude","CAP_FACE",FACE,{"disambiguationData":[OSD([sQuery(id+"F7.wireOp",EDGE,"E18.bottom"),sQuery(id+"F7.wireOp",EDGE,"E18.top"),sQuery(id+"F7.wireOp",EDGE,"E18.left"),sQuery(id+"F7.wireOp",EDGE,"E18.right"),sQuery(id+"F7.wireOp",EDGE,"E19")])],"isStart":false})]}),makeQuery(id+"F10.opExtrude","SWEPT_EDGE",EDGE,{"disambiguationData":[OSD([sQuery(id+"F9.wireOp",EDGE,"E22"),sQuery(id+"F9.wireOp",EDGE,"E23")])]})]});
            fillet(context, id + "F34", {"entities" : qUnion([Q0, Q1, Q2, Q3, Q4, Q5]), "radius" : 2 * mm, "tangentPropagation" : true, "allowEdgeOverflow" : false});
        }
        {
            var Q0;
            Q0=makeQuery(id+"F14.boolean.opBoolean","MERGE",FACE,{"derivedFrom":[makeQuery(id+"F8.opExtrude","CAP_FACE",FACE,{"disambiguationData":[OSD([sQuery(id+"F6.wireOp",EDGE,"E15"),sQuery(id+"F6.wireOp",EDGE,"E16.bottom"),sQuery(id+"F6.wireOp",EDGE,"E16.top"),sQuery(id+"F6.wireOp",EDGE,"E16.left"),sQuery(id+"F6.wireOp",EDGE,"E16.right")])],"isStart":true}),makeQuery(id+"F8.opExtrude","CAP_FACE",FACE,{"disambiguationData":[OSD([sQuery(id+"F7.wireOp",EDGE,"E18.bottom"),sQuery(id+"F7.wireOp",EDGE,"E18.top"),sQuery(id+"F7.wireOp",EDGE,"E18.left"),sQuery(id+"F7.wireOp",EDGE,"E18.right"),sQuery(id+"F7.wireOp",EDGE,"E19")])],"isStart":true}),makeQuery(id+"F14.opExtrude","CAP_FACE",FACE,{"disambiguationData":[OSD([sQuery(id+"F13.wireOp",EDGE,"E27.bottom"),sQuery(id+"F13.wireOp",EDGE,"E27.top"),sQuery(id+"F13.wireOp",EDGE,"E27.left"),sQuery(id+"F13.wireOp",EDGE,"E27.right")])],"isStart":true})]});
            var sketch = newSketch(context, id + "F35", { "sketchPlane" : qUnion([Q0])});
            skPoint(sketch, "E87", {"position": v(-50.65, 56.21) * mm});
            skPoint(sketch, "E88", {"position": v(-50.65, 88.21) * mm});
            skPoint(sketch, "E89", {"position": v(-50.65, 24.21) * mm});
            skLineSegment(sketch, "E90", {"start": v(-50.65, 88.21) * mm, "end": v(-50.65, 24.21) * mm});
            skSolve(sketch);
        }
        {
            var Q0;
            Q0=sQuery(id+"F35.wireOp",VERTEX,"E87");
            var Q1;
            Q1=qCreatedBy(makeId("Right.planeOp"),FACE);
            cPlane(context, id + "F36", {"entities" : qUnion([Q0, Q1]), "cplaneType" : CPlaneType.PLANE_POINT, "offset" : 25 * mm, "width" : 150 * mm, "height" : 150 * mm});
        }
        {
            var Q0;
            Q0=qCreatedBy(id+"F36.planeOp",FACE);
            var sketch = newSketch(context, id + "F37", { "sketchPlane" : qUnion([Q0])});
            skArc(sketch, "E91", {"start": v(-1.88, 36.12) * mm, "mid": v(1.16, 53.8) * mm, "end": v(10.24, 69.26) * mm});
            skArc(sketch, "E92.0", {"start": v(2.36, 31.88) * mm, "mid": v(4.18, 50.25) * mm, "end": v(13.08, 66.42) * mm});
            skLineSegment(sketch, "E93", {"start": v(13.08, 66.42) * mm, "end": v(10.24, 69.26) * mm});
            skLineSegment(sketch, "E94", {"start": v(20.75, 58.75) * mm, "end": v(10.24, 69.26) * mm, "construction": true});
            skLineSegment(sketch, "E95", {"start": v(-1.88, 36.12) * mm, "end": v(20.75, 58.75) * mm, "construction": true});
            skLineSegment(sketch, "E96", {"start": v(-1.88, 36.12) * mm, "end": v(2.36, 31.88) * mm});
            skSolve(sketch);
        }
        {
            var Q0;
            Q0 = qSketchRegion(id + "F37", true);
            var Q1;
            Q1=sQuery(id+"F37.wireOp",EDGE,"E94");
            revolve(context, id + "F38", {"operationType" : NewBodyOperationType.ADD, "entities" : qUnion([Q0]), "axis" : qUnion([Q1]), "revolveType" : RevolveType.FULL});
        }
    });
